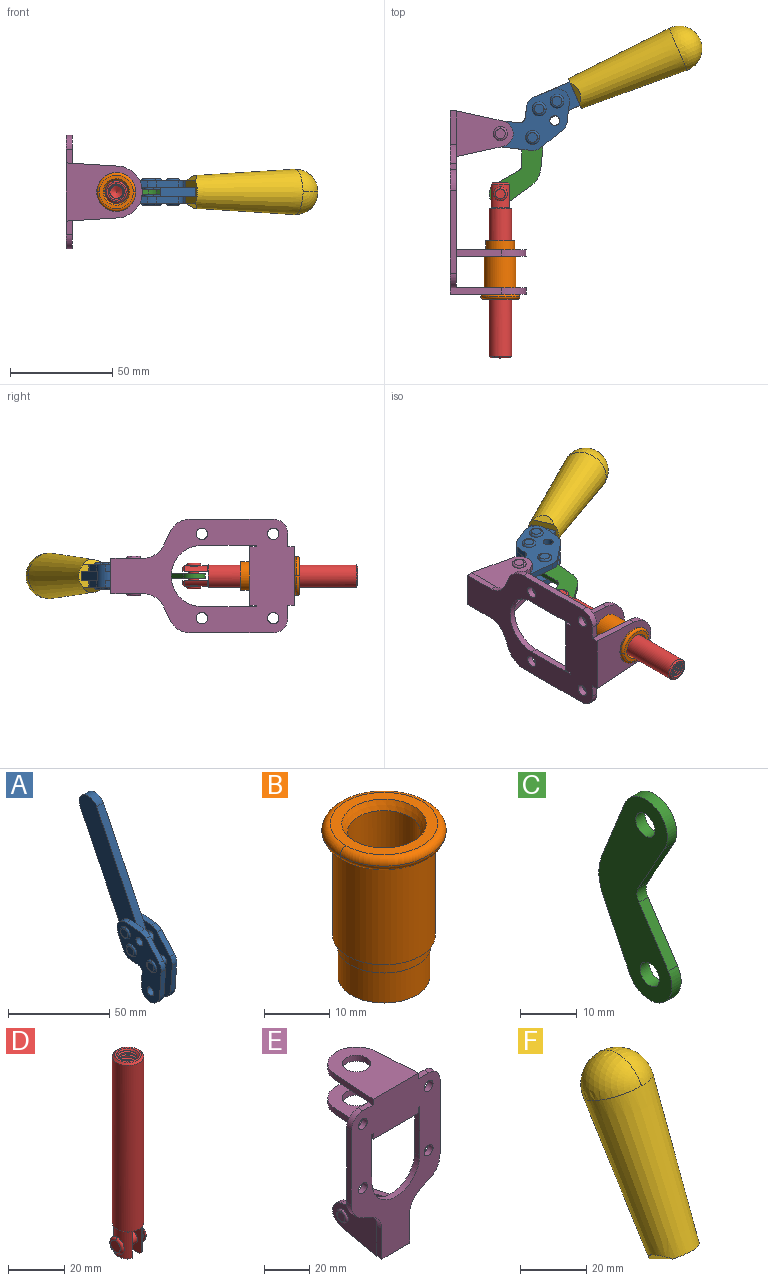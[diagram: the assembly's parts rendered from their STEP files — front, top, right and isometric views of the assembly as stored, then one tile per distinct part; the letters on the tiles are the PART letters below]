
ASSEMBLY  parts=6 mates=6
PART A: 59 faces, bbox 12.9x60.2x99.6 mm
  f0: torus R=2.39mm, axis (-1,0,0), area 14.9mm2, adj f20,f43,f51
  f1: torus R=2.39mm, axis (-1,0,0), area 14.9mm2, adj f19,f42,f51
  f2: torus R=2.39mm, axis (-1,0,0), area 14.9mm2, adj f18,f35,f51
  f3: torus R=2.39mm, axis (-1,0,0), area 14.9mm2, adj f14,f17,f23
  f4: torus R=2.39mm, axis (-1,0,0), area 14.9mm2, adj f13,f16,f23
  f5: torus R=2.39mm, axis (-1,0,0), area 14.9mm2, adj f12,f15,f23
  f6: cylinder r=2.39mm len=4.78mm, axis (1,0,0), area 46.5mm2, adj f48,f50,f51
  f7: cylinder r=2.39mm len=4.78mm, axis (1,0,0), area 46.5mm2, adj f50,f51
  f8: cylinder r=6.35mm len=12.68mm, axis (1,0,0), area 61.8mm2, adj f38,f39,f50,f51
  f9: cylinder r=2.39mm len=4.78mm, axis (-1,0,0), area 70.5mm2, adj f46,f50
  f10: cylinder r=2.39mm len=4.78mm, axis (-1,0,0), area 46.5mm2, adj f23,f45,f46
  f11: cylinder r=2.39mm len=4.78mm, axis (-1,0,0), area 46.5mm2, adj f23,f46
  f12: plane 4.78x4.78mm, normal (1,0,0), area 17.9mm2, adj f5,f15
  f13: plane 4.78x4.78mm, normal (1,0,0), area 17.9mm2, adj f4,f16
  f14: plane 4.78x4.78mm, normal (1,0,0), area 17.9mm2, adj f3,f17
  f15: torus R=2.39mm, axis (-1,0,0), area 14.9mm2, adj f5,f12,f23
  f16: torus R=2.39mm, axis (-1,0,0), area 14.9mm2, adj f4,f13,f23
  f17: torus R=2.39mm, axis (-1,0,0), area 14.9mm2, adj f3,f14,f23
  f18: plane 4.78x4.78mm, normal (-1,0,0), area 17.9mm2, adj f2,f35
  f19: plane 4.78x4.78mm, normal (-1,0,0), area 17.9mm2, adj f1,f42
  f20: plane 4.78x4.78mm, normal (-1,0,0), area 17.9mm2, adj f0,f43
  f21: plane 2.26x0.2mm, normal (1,0,0), area 0.2mm2, adj f31,f44
  f22: plane 2.26x0.2mm, normal (-1,0,0), area 0.2mm2, adj f41,f44
  f23: plane 39.37x30.77mm, normal (1,0,0), area 565.5mm2, adj f3,f4,f5,f10,f11,f15,f16,f17
  f24: cylinder r=6.1mm len=4.15mm, axis (-1,0,0), area 14.7mm2, adj f23,f25,f32,f46
  f25: plane 10.25x9.01mm, normal (0,-0.75,0.66), area 42.3mm2, adj f23,f24,f26,f46
  f26: cylinder r=6.35mm len=4.64mm, axis (-1,0,0), area 15.6mm2, adj f23,f25,f27,f46
  f27: plane 15.84x3.1mm, normal (0,-1,-0.07), area 49.2mm2, adj f23,f26,f28,f46
  f28: cylinder r=6.35mm len=12.68mm, axis (-1,0,0), area 61.8mm2, adj f23,f27,f29,f46
  f29: plane 8.11x3.1mm, normal (0,1,0.07), area 25.2mm2, adj f23,f28,f30,f46
  f30: cylinder r=3.05mm len=3.25mm, axis (-1,0,0), area 14.8mm2, adj f23,f29,f31,f46
  f31: plane 5.99x3.1mm, normal (0,0.07,-1), area 18.6mm2, adj f21,f23,f30,f44,f46
  f32: plane 9.5x3.1mm, normal (0,-0.07,1), area 29.5mm2, adj f23,f24,f33,f46,f47
  f33: cylinder r=6.1mm len=8.63mm, axis (-1,0,0), area 39.1mm2, adj f23,f32,f34,f47
  f34: plane 8.65x3.96mm, normal (0,0.91,-0.42), area 29.5mm2, adj f23,f33,f44,f47
  f35: torus R=2.39mm, axis (-1,0,0), area 14.9mm2, adj f2,f18,f51
  f36: plane 10.25x9.01mm, normal (0,-0.75,0.66), area 42.3mm2, adj f37,f49,f50,f51
  f37: cylinder r=6.35mm len=4.64mm, axis (1,0,0), area 15.6mm2, adj f36,f38,f50,f51
  f38: plane 15.84x3.1mm, normal (0,-1,-0.07), area 49.2mm2, adj f8,f37,f50,f51
  f39: plane 8.11x3.1mm, normal (0,1,0.07), area 25.2mm2, adj f8,f40,f50,f51
  f40: cylinder r=3.05mm len=3.25mm, axis (1,0,0), area 14.8mm2, adj f39,f41,f50,f51
  f41: plane 5.99x3.1mm, normal (0,0.07,-1), area 18.6mm2, adj f22,f40,f44,f50,f51
  f42: torus R=2.39mm, axis (-1,0,0), area 14.9mm2, adj f1,f19,f51
  f43: torus R=2.39mm, axis (-1,0,0), area 14.9mm2, adj f0,f20,f51
  f44: cylinder r=6.35mm len=12.12mm, axis (-1,0,0), area 128.9mm2, adj f21,f22,f23,f31,f34,f41,f46,f47
  f45: plane 2.65x1.35mm, normal (1,0,0), area 1mm2, adj f10,f55
  f46: plane 39.08x20.42mm, normal (-1,0,0), area 412.5mm2, adj f9,f10,f11,f24,f25,f26,f27,f28
  f47: plane 77.62x39.82mm, normal (1,0,0), area 850mm2, adj f32,f33,f34,f44,f53,f54,f55
  f48: plane 2.65x1.35mm, normal (-1,0,0), area 1mm2, adj f6,f55
  f49: cylinder r=6.1mm len=4.15mm, axis (1,0,0), area 14.7mm2, adj f36,f50,f51,f56
  f50: plane 39.08x20.42mm, normal (1,0,0), area 412.5mm2, adj f6,f7,f8,f9,f36,f37,f38,f39
  f51: plane 39.37x30.77mm, normal (-1,0,0), area 565.5mm2, adj f0,f1,f2,f6,f7,f8,f35,f36
  f52: plane 8.65x3.96mm, normal (0,0.91,-0.42), area 29.5mm2, adj f44,f51,f57,f58
  f53: plane 68.49x33.4mm, normal (0,0.9,-0.44), area 358.1mm2, adj f44,f47,f54,f58
  f54: cylinder r=6.35mm len=12.06mm, axis (1,0,0), area 93.7mm2, adj f47,f53,f55,f58
  f55: plane 68.49x33.4mm, normal (0,-0.9,0.44), area 358.1mm2, adj f44,f45,f46,f47,f48,f50,f54,f58
  f56: plane 9.5x3.1mm, normal (0,-0.07,1), area 29.5mm2, adj f49,f50,f51,f57,f58
  f57: cylinder r=6.1mm len=8.63mm, axis (1,0,0), area 39.1mm2, adj f51,f52,f56,f58
  f58: plane 77.62x39.82mm, normal (-1,0,0), area 850mm2, adj f44,f52,f53,f54,f55,f56,f57
PART B: 15 faces, bbox 20.6x20.6x28.7 mm
  f0: torus R=8.26mm, axis (0,0,1), area 56.8mm2, adj f1,f10,f12
  f1: torus R=8.26mm, axis (0,0,1), area 56.8mm2, adj f0,f6,f13
  f2: cylinder r=5.59mm len=25.91mm, axis (0,0,1), area 909.6mm2, adj f3,f4
  f3: cone r=6.86mm half-angle=45deg, axis (0,0,-1), area 70.2mm2, adj f2,f14
  f4: cone r=6.47mm half-angle=30deg, axis (0,0,1), area 66.7mm2, adj f2,f13
  f5: cylinder r=7.04mm len=14.07mm, axis (0,0,1), area 252.6mm2, adj f11,f14
  f6: torus R=8.26mm, axis (0,0,1), area 56.8mm2, adj f1,f12,f13
  f7: cylinder r=7.16mm len=14.33mm, axis (0,0,1), area 91.5mm2, adj f9,f11
  f8: cylinder r=7.86mm len=18.42mm, axis (0,0,1), area 909.6mm2, adj f9,f10
  f9: plane 15.72x15.72mm, normal (0,0,-1), area 33mm2, adj f7,f8
  f10: plane 16.51x16.51mm, normal (0,0,-1), area 19.9mm2, adj f0,f8,f12
  f11: plane 14.33x14.33mm, normal (0,0,-1), area 5.7mm2, adj f5,f7
  f12: torus R=8.26mm, axis (0,0,1), area 56.8mm2, adj f0,f6,f10
  f13: plane 16.51x16.51mm, normal (0,0,1), area 82.7mm2, adj f1,f4,f6
  f14: plane 14.07x14.07mm, normal (0,0,-1), area 7.8mm2, adj f3,f5
PART C: 12 faces, bbox 2.3x18.2x42.8 mm
  f0: cylinder r=2.4mm len=4.8mm, axis (1,0,0), area 34.9mm2, adj f4,f11
  f1: cylinder r=10.41mm len=8.47mm, axis (1,0,0), area 20.2mm2, adj f4,f9,f10,f11
  f2: cylinder r=3.05mm len=3.16mm, axis (1,0,0), area 7.7mm2, adj f4,f6,f7,f11
  f3: cylinder r=2.4mm len=4.8mm, axis (1,0,0), area 34.9mm2, adj f4,f11
  f4: plane 42.81x18.23mm, normal (-1,0,0), area 414.1mm2, adj f0,f1,f2,f3,f5,f6,f7,f8
  f5: cylinder r=5.54mm len=10.67mm, axis (1,0,0), area 41.8mm2, adj f4,f6,f10,f11
  f6: plane 11.66x6.53mm, normal (0,-0.87,-0.49), area 30.9mm2, adj f2,f4,f5,f11
  f7: plane 11.17x7.33mm, normal (0,-0.84,0.55), area 30.9mm2, adj f2,f4,f8,f11
  f8: cylinder r=5.54mm len=10.51mm, axis (1,0,0), area 41.8mm2, adj f4,f7,f9,f11
  f9: plane 13.67x6.67mm, normal (0,0.9,-0.44), area 35.1mm2, adj f1,f4,f8,f11
  f10: plane 14.1x5.7mm, normal (0,0.93,0.37), area 35.1mm2, adj f1,f4,f5,f11
  f11: plane 42.81x18.23mm, normal (1,0,0), area 414.1mm2, adj f0,f1,f2,f3,f5,f6,f7,f8
PART D: 48 faces, bbox 12.6x11.1x86.1 mm
  f0: torus R=2.41mm, axis (-1,0,0), area 15mm2, adj f30,f32,f34
  f1: torus R=2.41mm, axis (-1,0,0), area 15mm2, adj f29,f31,f33
  f2: cylinder r=5.54mm len=72.39mm, axis (0,0,1), area 2518.5mm2, adj f3,f4,f42,f43
  f3: cone r=5.54mm half-angle=45deg, axis (0,0,1), area 7.6mm2, adj f2,f5,f41
  f4: cone r=5.54mm half-angle=45deg, axis (0,0,-1), area 34.9mm2, adj f2,f39
  f5: cylinder r=5.08mm len=11.48mm, axis (0,0,1), area 108.3mm2, adj f3,f7,f8,f41
  f6: cylinder r=2.41mm len=4.83mm, axis (-1,0,0), area 71.2mm2, adj f40,f41
  f7: cylinder r=2.41mm len=4.83mm, axis (-1,0,0), area 7.6mm2, adj f5,f34
  f8: cone r=5.08mm half-angle=45deg, axis (0,0,1), area 10.6mm2, adj f5,f37,f41
  f9: cone r=3.98mm half-angle=45deg, axis (0,0,1), area 17.6mm2, adj f27,f39,f45,f46,f47
  f10: cylinder r=2.41mm len=4.83mm, axis (-1,0,0), area 7.6mm2, adj f33,f38
  f11: cylinder r=3.2mm len=6.4mm, axis (0,0,1), area 78.4mm2, adj f12,f28,f44,f45,f47
  f12: cylinder r=3.2mm len=6.4mm, axis (0,0,1), area 10.5mm2, adj f11,f13,f45,f47
  f13: cylinder r=3.2mm len=6.4mm, axis (0,0,1), area 10.5mm2, adj f12,f14,f45,f47
  f14: cylinder r=3.2mm len=6.4mm, axis (0,0,1), area 10.5mm2, adj f13,f15,f45,f47
  f15: cylinder r=3.2mm len=6.4mm, axis (0,0,1), area 10.5mm2, adj f14,f16,f45,f47
  f16: cylinder r=3.2mm len=6.4mm, axis (0,0,1), area 10.5mm2, adj f15,f17,f45,f47
  f17: cylinder r=3.2mm len=6.4mm, axis (0,0,1), area 10.5mm2, adj f16,f18,f45,f47
  f18: cylinder r=3.2mm len=6.4mm, axis (0,0,1), area 10.5mm2, adj f17,f19,f45,f47
  f19: cylinder r=3.2mm len=6.4mm, axis (0,0,1), area 10.5mm2, adj f18,f20,f45,f47
  f20: cylinder r=3.2mm len=6.4mm, axis (0,0,1), area 10.5mm2, adj f19,f21,f45,f47
  f21: cylinder r=3.2mm len=6.4mm, axis (0,0,1), area 10.5mm2, adj f20,f22,f45,f47
  f22: cylinder r=3.2mm len=6.4mm, axis (0,0,1), area 10.5mm2, adj f21,f23,f45,f47
  f23: cylinder r=3.2mm len=6.4mm, axis (0,0,1), area 10.5mm2, adj f22,f24,f45,f47
  f24: cylinder r=3.2mm len=6.4mm, axis (0,0,1), area 10.5mm2, adj f23,f25,f45,f47
  f25: cylinder r=3.2mm len=6.4mm, axis (0,0,1), area 10.5mm2, adj f24,f26,f45,f47
  f26: cylinder r=3.2mm len=6.4mm, axis (0,0,1), area 10.5mm2, adj f25,f27,f45,f47
  f27: cylinder r=3.2mm len=6.4mm, axis (0,0,1), area 7.4mm2, adj f9,f26,f45,f47
  f28: cone r=3.2mm half-angle=60deg, axis (0,0,1), area 37.2mm2, adj f11
  f29: plane 4.83x4.83mm, normal (-1,0,0), area 18.3mm2, adj f1,f31
  f30: plane 4.83x4.83mm, normal (1,0,0), area 18.3mm2, adj f0,f32
  f31: torus R=2.41mm, axis (-1,0,0), area 15mm2, adj f1,f29,f33
  f32: torus R=2.41mm, axis (-1,0,0), area 15mm2, adj f0,f30,f34
  f33: plane 6.83x6.83mm, normal (1,0,0), area 18.3mm2, adj f1,f10,f31
  f34: plane 6.83x6.83mm, normal (-1,0,0), area 18.3mm2, adj f0,f7,f32
  f35: cone r=5.08mm half-angle=45deg, axis (0,0,1), area 10.6mm2, adj f36,f38,f40
  f36: plane 7.25x1.97mm, normal (0,0,-1), area 10mm2, adj f35,f40
  f37: plane 7.25x1.97mm, normal (0,0,-1), area 10mm2, adj f8,f41
  f38: cylinder r=5.08mm len=11.48mm, axis (0,0,1), area 108.3mm2, adj f10,f35,f40,f42
  f39: plane 9.55x9.55mm, normal (0,0,1), area 22mm2, adj f4,f9
  f40: plane 12.76x10.09mm, normal (1,0,0), area 95.7mm2, adj f6,f35,f36,f38,f42,f43
  f41: plane 12.76x10.09mm, normal (-1,0,0), area 95.7mm2, adj f3,f5,f6,f8,f37,f43
  f42: cone r=5.54mm half-angle=45deg, axis (0,0,1), area 7.6mm2, adj f2,f38,f40
  f43: plane 11.07x4.7mm, normal (0,0,-1), area 50.4mm2, adj f2,f40,f41
  f44: plane 0.89x0.62mm, normal (-1,0,0), area 0.3mm2, adj f11,f45,f46,f47
  f45: bspline ~24.8x7.63mm, area 266.6mm2, adj f9,f11,f12,f13,f14,f15,f16,f17
  f46: bspline ~24.87x7.63mm, area 73.6mm2, adj f9,f44,f45,f47
  f47: bspline ~24.98x7.63mm, area 272.5mm2, adj f9,f11,f12,f13,f14,f15,f16,f17
PART E: 55 faces, bbox 55.7x37.4x89.8 mm
  f0: torus R=2.41mm, axis (-1,0,0), area 15mm2, adj f11,f15,f25
  f1: torus R=2.41mm, axis (-1,0,0), area 15mm2, adj f10,f12,f22
  f2: cylinder r=2.78mm len=5.56mm, axis (0,-1,0), area 54.2mm2, adj f30,f54
  f3: cylinder r=14.99mm len=29.97mm, axis (0,-1,0), area 145.9mm2, adj f30,f49,f53,f54
  f4: cylinder r=2.78mm len=5.56mm, axis (0,-1,0), area 54.2mm2, adj f30,f54
  f5: cylinder r=2.78mm len=5.56mm, axis (0,-1,0), area 54.2mm2, adj f30,f54
  f6: cylinder r=2.78mm len=5.56mm, axis (0,-1,0), area 54.2mm2, adj f30,f54
  f7: cylinder r=6.35mm len=12.7mm, axis (0,0,1), area 123.6mm2, adj f27,f51
  f8: cylinder r=6.35mm len=12.7mm, axis (0,0,-1), area 124.7mm2, adj f21,f35
  f9: cylinder r=2.41mm len=11.18mm, axis (-1,0,0), area 169.4mm2, adj f16,f19
  f10: plane 4.83x4.83mm, normal (1,0,0), area 18.3mm2, adj f1,f12
  f11: plane 4.83x4.83mm, normal (-1,0,0), area 18.3mm2, adj f0,f15
  f12: torus R=2.41mm, axis (-1,0,0), area 15mm2, adj f1,f10,f22
  f13: cylinder r=6.35mm len=12.41mm, axis (1,0,0), area 53.4mm2, adj f18,f19,f22,f23
  f14: cylinder r=6.35mm len=12.41mm, axis (-1,0,0), area 53.4mm2, adj f16,f17,f24,f25
  f15: torus R=2.41mm, axis (-1,0,0), area 15mm2, adj f0,f11,f25
  f16: plane 27.86x22.35mm, normal (1,0,0), area 425.4mm2, adj f9,f14,f17,f24,f30
  f17: plane 22.86x4.97mm, normal (0,0.21,0.98), area 72.5mm2, adj f14,f16,f25,f30
  f18: plane 22.86x4.97mm, normal (0,0.21,0.98), area 72.5mm2, adj f13,f19,f22,f30
  f19: plane 27.86x22.35mm, normal (-1,0,0), area 425.4mm2, adj f9,f13,f18,f23,f30
  f20: cylinder r=12.7mm len=25.35mm, axis (0,0,-1), area 119.8mm2, adj f21,f34,f35,f36
  f21: plane 34.21x28.07mm, normal (0,0,-1), area 702.4mm2, adj f8,f20,f30,f34,f36
  f22: plane 27.96x22.45mm, normal (1,0,0), area 407.2mm2, adj f1,f12,f13,f18,f23,f30,f42,f43
  f23: plane 22.86x4.97mm, normal (0,0.21,-0.98), area 72.5mm2, adj f13,f19,f22,f44
  f24: plane 22.86x4.97mm, normal (0,0.21,-0.98), area 72.5mm2, adj f14,f16,f25,f44
  f25: plane 27.86x22.35mm, normal (-1,0,0), area 407.1mm2, adj f0,f14,f15,f17,f24,f30,f45,f46
  f26: plane 3.1x0.95mm, normal (0,0,-1), area 2.7mm2, adj f30,f49,f50,f54
  f27: plane 34.21x28.07mm, normal (0,0,1), area 702.4mm2, adj f7,f28,f30,f50,f52
  f28: cylinder r=12.7mm len=25.35mm, axis (0,0,1), area 118.8mm2, adj f27,f50,f51,f52
  f29: plane 3.1x0.95mm, normal (0,0,-1), area 2.7mm2, adj f30,f52,f53,f54
  f30: plane 86.54x55.63mm, normal (0,1,0), area 2362.9mm2, adj f2,f3,f4,f5,f6,f16,f17,f18
  f31: plane 40.56x3.1mm, normal (-1,0,0), area 125.7mm2, adj f30,f32,f48,f54
  f32: cylinder r=7.11mm len=7.11mm, axis (0,-1,0), area 34.6mm2, adj f30,f31,f33,f54
  f33: plane 6.67x3.1mm, normal (0,0,1), area 20.4mm2, adj f30,f32,f34,f54
  f34: plane 25.39x3.13mm, normal (-1,0.06,0), area 79.5mm2, adj f20,f21,f33,f35,f54
  f35: plane 37.31x28.45mm, normal (0,0,1), area 789.9mm2, adj f8,f20,f34,f36,f54
  f36: plane 25.39x3.13mm, normal (1,0.06,0), area 79.5mm2, adj f20,f21,f35,f37,f54
  f37: plane 6.67x3.1mm, normal (0,0,1), area 20.4mm2, adj f30,f36,f38,f54
  f38: cylinder r=7.11mm len=7.11mm, axis (0,-1,0), area 34.6mm2, adj f30,f37,f39,f54
  f39: plane 40.56x3.1mm, normal (1,0,0), area 125.7mm2, adj f30,f38,f40,f54
  f40: cylinder r=11.18mm len=10.16mm, axis (0,-1,0), area 39.5mm2, adj f30,f39,f41,f54
  f41: plane 6.09x3.1mm, normal (0.42,0,-0.91), area 20.8mm2, adj f30,f40,f42,f54
  f42: cylinder r=11.18mm len=9.41mm, axis (0,-1,0), area 37.2mm2, adj f22,f30,f41,f43,f54
  f43: plane 16.5x3.1mm, normal (1,0,0), area 51.1mm2, adj f22,f42,f44,f54
  f44: plane 17.37x3.1mm, normal (0,0,-1), area 53.8mm2, adj f23,f24,f30,f43,f45,f54
  f45: plane 16.5x3.1mm, normal (-1,0,0), area 51.1mm2, adj f25,f44,f46,f54
  f46: cylinder r=11.18mm len=9.41mm, axis (0,-1,0), area 37.2mm2, adj f25,f30,f45,f47,f54
  f47: plane 6.09x3.1mm, normal (-0.42,0,-0.91), area 20.8mm2, adj f30,f46,f48,f54
  f48: cylinder r=11.18mm len=10.16mm, axis (0,-1,0), area 39.5mm2, adj f30,f31,f47,f54
  f49: plane 26.54x3.1mm, normal (-1,0,0), area 82.3mm2, adj f3,f26,f30,f54
  f50: plane 25.39x3.1mm, normal (1,0.06,0), area 78.8mm2, adj f26,f27,f28,f51,f54
  f51: plane 37.31x28.45mm, normal (0,0,-1), area 789.9mm2, adj f7,f28,f50,f52,f54
  f52: plane 25.39x3.1mm, normal (-1,0.06,0), area 78.8mm2, adj f27,f28,f29,f51,f54
  f53: plane 26.54x3.1mm, normal (1,0,0), area 82.3mm2, adj f3,f29,f30,f54
  f54: plane 89.66x55.63mm, normal (0,-1,0), area 2678.5mm2, adj f2,f3,f4,f5,f6,f26,f29,f31
PART F: 11 faces, bbox 22.3x42.6x64.5 mm
  f0: sphere r=11.13mm, area 411.4mm2, adj f1,f8
  f1: cone r=11.11mm half-angle=3.3deg, axis (0,0.44,0.9), area 3251.8mm2, adj f0,f7,f8,f9,f10
  f2: cylinder r=6.16mm len=11.7mm, axis (1,0,0), area 89.5mm2, adj f3,f4,f5,f6
  f3: plane 60.23x36.75mm, normal (-1,0,0), area 763.6mm2, adj f2,f4,f6,f10
  f4: plane 51.37x25.05mm, normal (0,0.9,-0.44), area 264.2mm2, adj f2,f3,f5,f10
  f5: plane 60.23x36.75mm, normal (1,0,0), area 763.6mm2, adj f2,f4,f6,f10
  f6: plane 51.37x25.05mm, normal (0,-0.9,0.44), area 264.2mm2, adj f2,f3,f5,f10
  f7: plane 9.95x5.95mm, normal (0.71,-0.31,-0.64), area 25.8mm2, adj f1,f10
  f8: sphere r=11.13mm, area 411.4mm2, adj f0,f1
  f9: plane 9.95x5.95mm, normal (-0.71,-0.31,-0.64), area 25.8mm2, adj f1,f10
  f10: plane 14.27x11.38mm, normal (0,-0.44,-0.9), area 106.7mm2, adj f1,f3,f4,f5,f6,f7,f9
PLACE A rot(axis=(0.02,1,-0.02),90deg) t=(36.83,7.53,0)mm
PLACE B rot(axis=(0,-0.71,0.71),180deg) t=(5.96,1.56,24.61)mm
PLACE C rot(axis=(0.66,0.37,-0.66),139.8deg) t=(-6.82,30.34,0)mm
PLACE D rot(axis=(0.58,0.58,-0.58),120deg) t=(-18.66,19.7,0)mm
PLACE E rot(axis=(0.58,0.58,-0.58),120deg) t=(-18.66,1.56,0)mm fixed
PLACE F rot(axis=(0.02,1,-0.02),90deg) t=(36.83,7.53,0.04)mm
MATE slider D.f2 <-> B.f2  axis (0,-1,0) through (5.96,-39.08,0)mm
MATE fastened A.f54 <-> F.f2  axis (0,0,1) through (94.95,75.86,2.35)mm
MATE revolute A.f7 <-> E.f0  axis (0,0,1) through (5.96,33.65,0)mm
MATE fastened B.f2 <-> E.f7  axis (0,1,0) through (5.96,-44.83,0)mm
MATE revolute C.f3 <-> A.f4  axis (0,0,-1) through (21.72,31.79,0)mm
MATE revolute C.f5 <-> D.f6  axis (0,0,-1) through (5.96,4.23,0)mm
